# Revit family: Support-Teknion-HWBFYS_hiSpace_Single_Sided_Frame-R2020
name_source: partatom
category: Furniture
units: mm (PartAtom-declared; Revit-internal decimal feet)

## family parameters
Always vertical = Yes
Cut with Voids When Loaded = No
OmniClass Number = 23.40.20.00
OmniClass Title = General Furniture and Specialties
Room Calculation Point = No
Shared = Yes
Work Plane-Based = No

## types (6) — shared parameters
Assembly Code = E2020200
Manufacturer = Teknion
Manufacturer Fax = 416.661.4586
Part Number = HWBFYS
Product Documentation Link = https://www.teknion.com
Product Line = hiSpace Single-Side Bench
Product Page URL = https://www.teknion.com
Series = Height-Adjustable Bench hiSpace
Sustainability Data = https://www.teknion.com
URL = www.teknion.com
Unit Weight URL = http://www.teknion.com
Warranty = http://www.teknion.com
zero-valued in all types: Default Elevation

## per-type parameters (varying)
| type | 24" Depth, Display with Up/Down Memory | 24" Depth, Toggle Display with Memory | 30" Depth, Display with Up/Down Memory | 30" Depth, Toggle Display with Memory | Center Gap | Description | Display with Up/Down Memory | Height | Leg Gap | Leg Height | Model | Toggle Display with Memory |
| Extended Electric - Extended, 24 Depth, Display with Up/Down Memory | Yes | No | No | No | 0 " | hiSpace Single-Sided Frame, Extended Electric - Extended, 24 Depth, Display with Up/Down Memory | Yes | 32.5 " | 0 " | 18.543 " | HWBFYS9E24_D | No |
| Extended Electric - Extended, 30 Depth, Display with Up/Down Memory | No | No | Yes | No | 0 " | hiSpace Single-Sided Frame, Extended Electric - Extended, 30 Depth, Display with Up/Down Memory | Yes | 29 " | 4.138 " | 18.543 " | HWBFYS9E30_D | No |
| Fixed Height, 24 Depth | No | No | No | No | 1.467 " | hiSpace Single-Sided Frame, Fixed Height, 24 Depth, No Switch | No | 29 " | 1.604 " | 24.299 " | HWBFYS2F24_N | No |
| Fixed Height, 30 Depth | No | No | No | No | 1.467 " | hiSpace Single-Sided Frame, Fixed Height, 30 Depth, No Switch | No | 29 " | 5.602 " | 24.299 " | HWBFYS2F30_N | No |
| Extended Electric - Extended, 24 Depth, Toggle Display with Memory | No | Yes | No | No | 0 " | hiSpace Single-Sided Frame, Extended Electric - Extended, 24 Depth, Toggle Display with Memory | No | 28.059 " | 0 " | 18.543 " | HWBFYS9E24_A | Yes |
| Extended Electric - Extended, 30 Depth, Toggle Display with Memory | No | No | No | Yes | 0 " | hiSpace Single-Sided Frame, Extended Electric - Extended, 30 Depth, Toggle Display with Memory | No | 35 " | 4.138 " | 18.543 " | HWBFYS9E30_A | Yes |

## geometry (parser evidence)
native form markers: Sweep x3
no freeform markers — native parametric forms only
